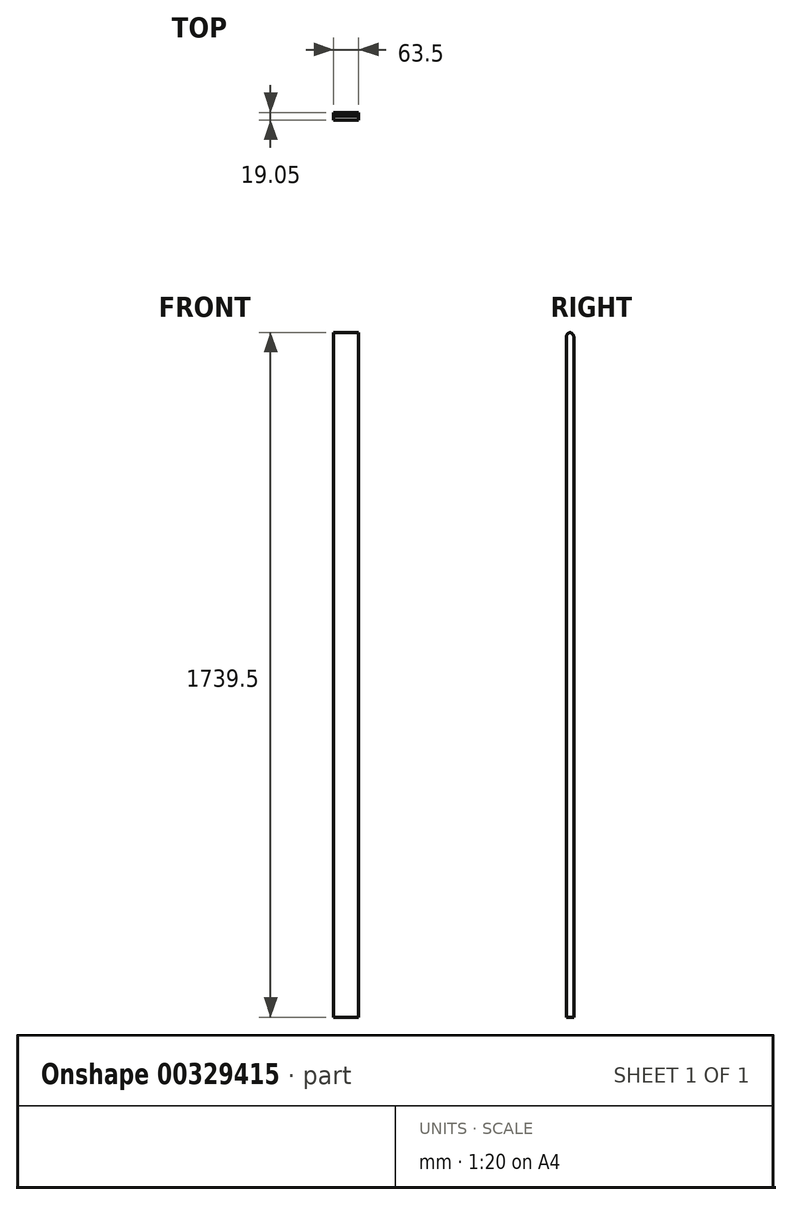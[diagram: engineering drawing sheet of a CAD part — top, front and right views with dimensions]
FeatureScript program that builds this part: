
annotation { "Feature Type Name" : "Feature", "Feature Type Description" : "" }
export const myFeature = defineFeature(function(context is Context, id is Id, definition is map)
    precondition{}
    {
        {
            var Q0;
            Q0=qCreatedBy(makeId("Front.planeOp"),FACE);
            var sketch = newSketch(context, id + "F0", { "sketchPlane" : qUnion([Q0])});
            skLineSegment(sketch, "E0.bottom", {"start": v(31.75, -869.95) * mm, "end": v(-31.75, -869.95) * mm});
            skLineSegment(sketch, "E0.top", {"start": v(31.75, 869.95) * mm, "end": v(-31.75, 869.95) * mm});
            skLineSegment(sketch, "E0.left", {"start": v(31.75, -869.95) * mm, "end": v(31.75, 869.95) * mm});
            skLineSegment(sketch, "E0.right", {"start": v(-31.75, -869.95) * mm, "end": v(-31.75, 869.95) * mm});
            skPoint(sketch, "E0.middle", {"position": v(0, 0) * mm});
            skSolve(sketch);
        }
        {
            var Q0;
            Q0 = qSketchRegion(id + "F0", true);
            extrude(context, id + "F1", {"entities" : qUnion([Q0]), "depth" : 19.05 * mm});
        }
        {
            var Q0;
            Q0=makeQuery(id+"F1.opExtrude","CAP_EDGE",EDGE,{"disambiguationData":[OSD([sQuery(id+"F0.wireOp",EDGE,"E0.top")])],"isStart":false});
            var Q1;
            Q1=makeQuery(id+"F1.opExtrude","CAP_EDGE",EDGE,{"disambiguationData":[OSD([sQuery(id+"F0.wireOp",EDGE,"E0.top")])],"isStart":true});
            fillet(context, id + "F2", {"entities" : qUnion([Q0, Q1]), "radius" : 12.7 * mm, "tangentPropagation" : true, "allowEdgeOverflow" : false});
        }
    });
